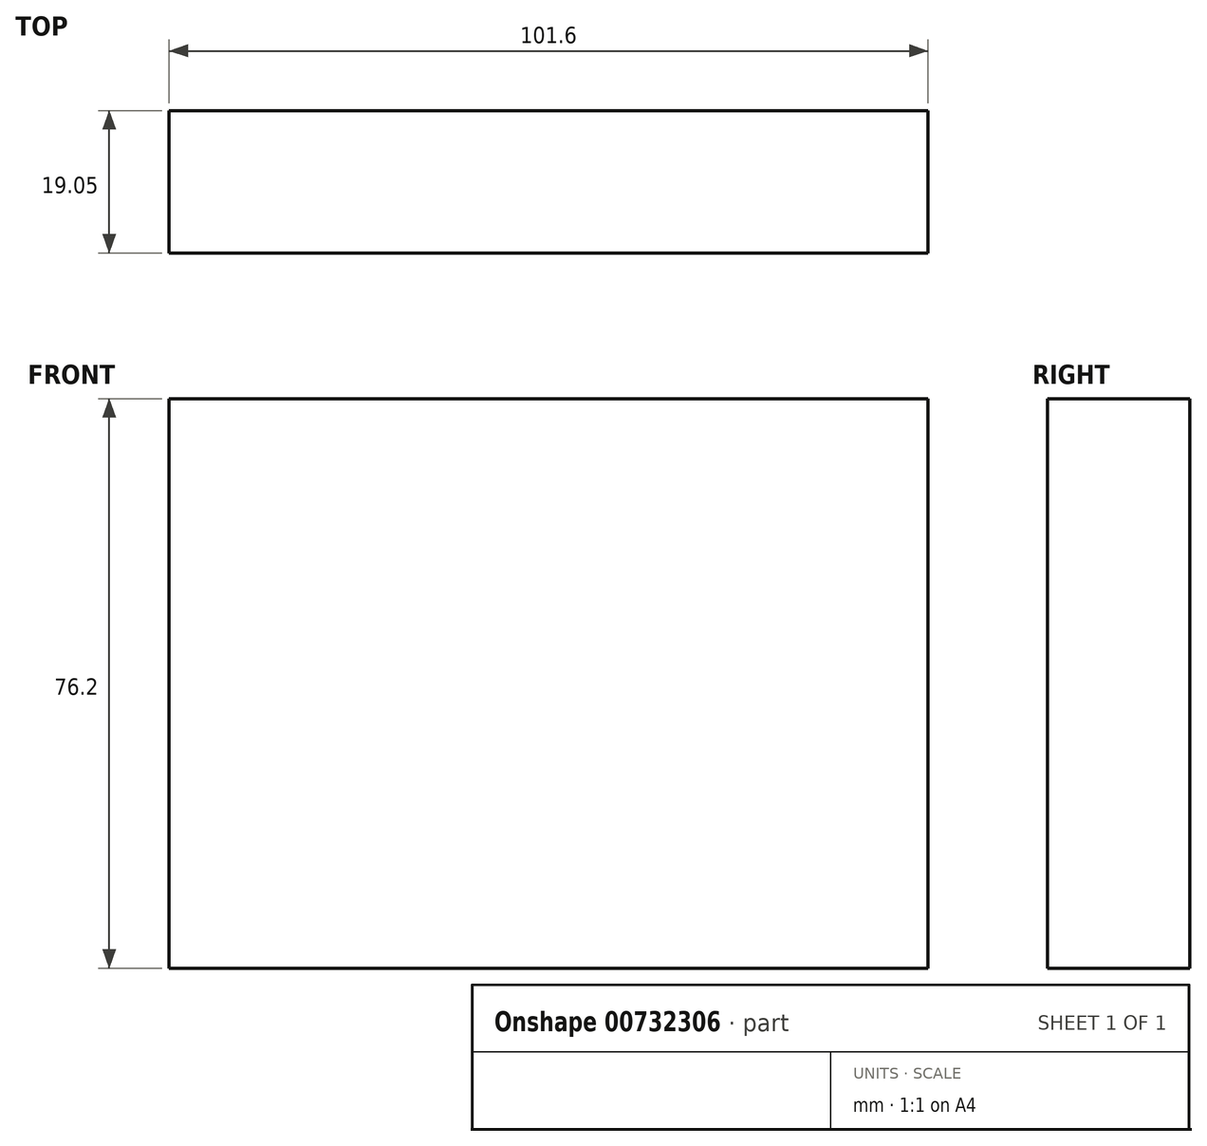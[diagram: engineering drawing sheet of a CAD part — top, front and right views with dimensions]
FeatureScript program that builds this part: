
annotation { "Feature Type Name" : "Feature", "Feature Type Description" : "" }
export const myFeature = defineFeature(function(context is Context, id is Id, definition is map)
    precondition{}
    {
        {
            var Q0;
            Q0=qCreatedBy(makeId("Front.planeOp"),FACE);
            var sketch = newSketch(context, id + "F0", { "sketchPlane" : qUnion([Q0])});
            skLineSegment(sketch, "E0.bottom", {"start": v(0, 0) * mm, "end": v(101.6, 0) * mm});
            skLineSegment(sketch, "E0.top", {"start": v(0, 76.2) * mm, "end": v(101.6, 76.2) * mm});
            skLineSegment(sketch, "E0.left", {"start": v(0, 0) * mm, "end": v(0, 76.2) * mm});
            skLineSegment(sketch, "E0.right", {"start": v(101.6, 0) * mm, "end": v(101.6, 76.2) * mm});
            skSolve(sketch);
        }
        {
            var Q0;
            Q0 = qSketchRegion(id + "F0", true);
            extrude(context, id + "F1", {"entities" : qUnion([Q0]), "depth" : 19.05 * mm, "offsetDistance" : 25.4 * mm});
        }
    });
